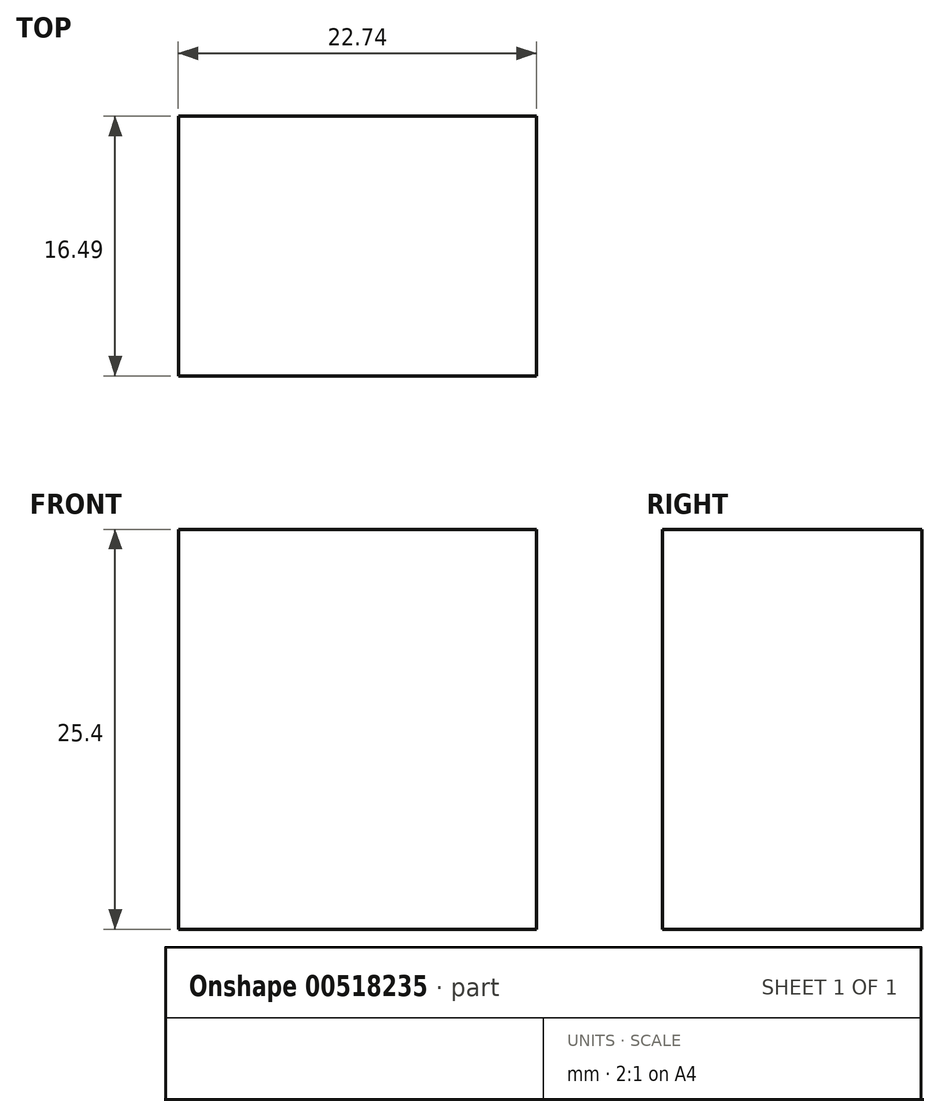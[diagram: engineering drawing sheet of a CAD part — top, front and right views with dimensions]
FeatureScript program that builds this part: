
annotation { "Feature Type Name" : "Feature", "Feature Type Description" : "" }
export const myFeature = defineFeature(function(context is Context, id is Id, definition is map)
    precondition{}
    {
        {
            var Q0;
            Q0=qCreatedBy(makeId("Top.planeOp"),FACE);
            var sketch = newSketch(context, id + "F0", { "sketchPlane" : qUnion([Q0])});
            skLineSegment(sketch, "E0.bottom", {"start": v(0, 0) * mm, "end": v(-22.74, 0) * mm});
            skLineSegment(sketch, "E0.top", {"start": v(0, -16.49) * mm, "end": v(-22.74, -16.49) * mm});
            skLineSegment(sketch, "E0.left", {"start": v(0, 0) * mm, "end": v(0, -16.49) * mm});
            skLineSegment(sketch, "E0.right", {"start": v(-22.74, 0) * mm, "end": v(-22.74, -16.49) * mm});
            skSolve(sketch);
        }
        {
            var Q0;
            Q0 = qSketchRegion(id + "F0", true);
            extrude(context, id + "F1", {"entities" : qUnion([Q0]), "depth" : 25.4 * mm, "offsetDistance" : 25.4 * mm});
        }
    });
